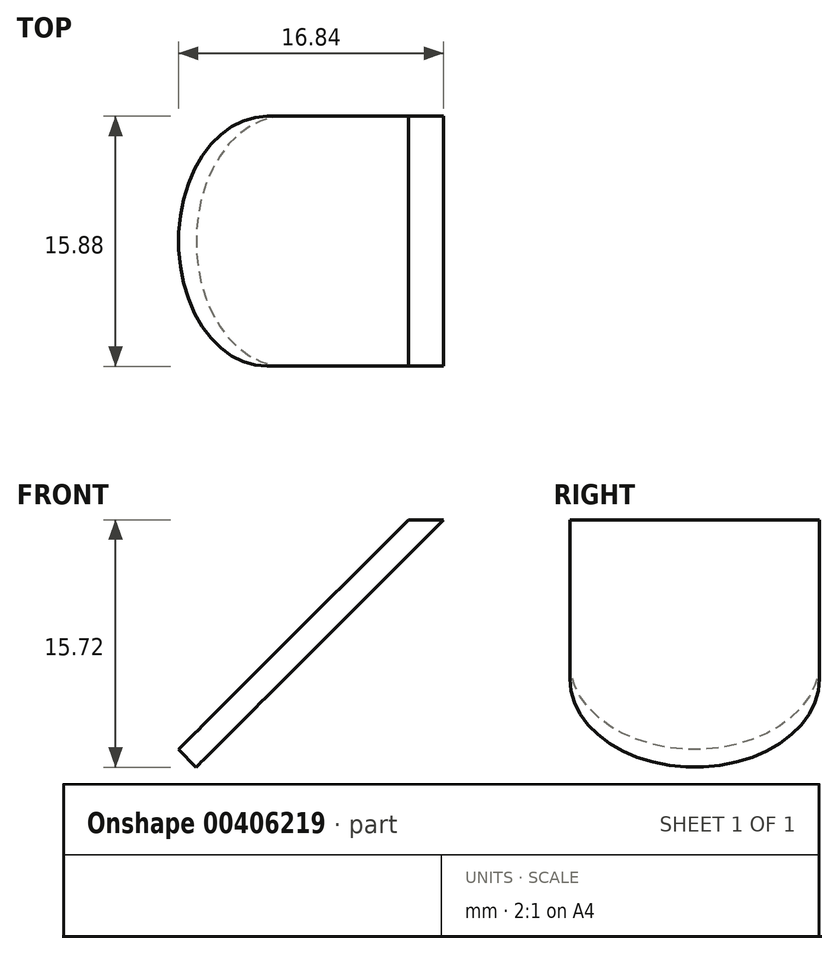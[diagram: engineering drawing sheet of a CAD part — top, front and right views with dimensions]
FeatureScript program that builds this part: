
annotation { "Feature Type Name" : "Feature", "Feature Type Description" : "" }
export const myFeature = defineFeature(function(context is Context, id is Id, definition is map)
    precondition{}
    {
        {
            var Q0;
            Q0=qCreatedBy(makeId("Front.planeOp"),FACE);
            var sketch = newSketch(context, id + "F0", { "sketchPlane" : qUnion([Q0])});
            skLineSegment(sketch, "E0", {"start": v(0, 0) * mm, "end": v(-14.6, -14.6) * mm});
            skLineSegment(sketch, "E1", {"start": v(-14.6, -14.6) * mm, "end": v(-13.47, -15.72) * mm});
            skLineSegment(sketch, "E2", {"start": v(-13.47, -15.72) * mm, "end": v(2.25, 0) * mm});
            skLineSegment(sketch, "E3", {"start": v(2.25, 0) * mm, "end": v(0, 0) * mm});
            skSolve(sketch);
        }
        {
            var Q0;
            Q0=makeQuery(id+"F0.imprint","IMPRINT",FACE,{"disambiguationData":[TD([[makeQuery(id+"F0.imprint","IMPRINT",EDGE,{"derivedFrom":sQuery(id+"F0.wireOp",EDGE,"E0")}),1.0]])]});
            extrude(context, id + "F1", {"entities" : qUnion([Q0]), "depth" : 15.88 * mm, "offsetDistance" : 25.4 * mm});
        }
        {
            var Q0;
            Q0=makeQuery(id+"F1.opExtrude","SWEPT_FACE",FACE,{"disambiguationData":[OSD([sQuery(id+"F0.wireOp",EDGE,"E0")])]});
            var sketch = newSketch(context, id + "F2", { "sketchPlane" : qUnion([Q0])});
            skArc(sketch, "E4", {"start": v(0, -12.7) * mm, "mid": v(7.94, -20.64) * mm, "end": v(15.88, -12.7) * mm});
            skLineSegment(sketch, "E5", {"start": v(0, -12.7) * mm, "end": v(0, -20.64) * mm});
            skLineSegment(sketch, "E6", {"start": v(0, -20.64) * mm, "end": v(15.88, -20.64) * mm});
            skLineSegment(sketch, "E7", {"start": v(15.88, -20.64) * mm, "end": v(15.88, -12.7) * mm});
            skSolve(sketch);
        }
        {
            var Q0;
            {var subQ0=sQuery(id+"F2.wireOp",EDGE,"E5");Q0=makeQuery(id+"F2.imprint","IMPRINT",FACE,{"disambiguationData":[TD([[makeQuery(id+"F2.imprint","IMPRINT",EDGE,{"derivedFrom":subQ0}),1.0]])]});}
            var Q1;
            {var subQ0=sQuery(id+"F2.wireOp",EDGE,"E7");Q1=makeQuery(id+"F2.imprint","IMPRINT",FACE,{"disambiguationData":[TD([[makeQuery(id+"F2.imprint","IMPRINT",EDGE,{"derivedFrom":subQ0}),-1.0]])]});}
            extrude(context, id + "F3", {"entities" : qUnion([Q0, Q1]), "operationType" : NewBodyOperationType.REMOVE, "endBound" : BoundingType.THROUGH_ALL, "oppositeDirection" : true, "depth" : 25.4 * mm, "offsetDistance" : 25.4 * mm});
        }
    });
